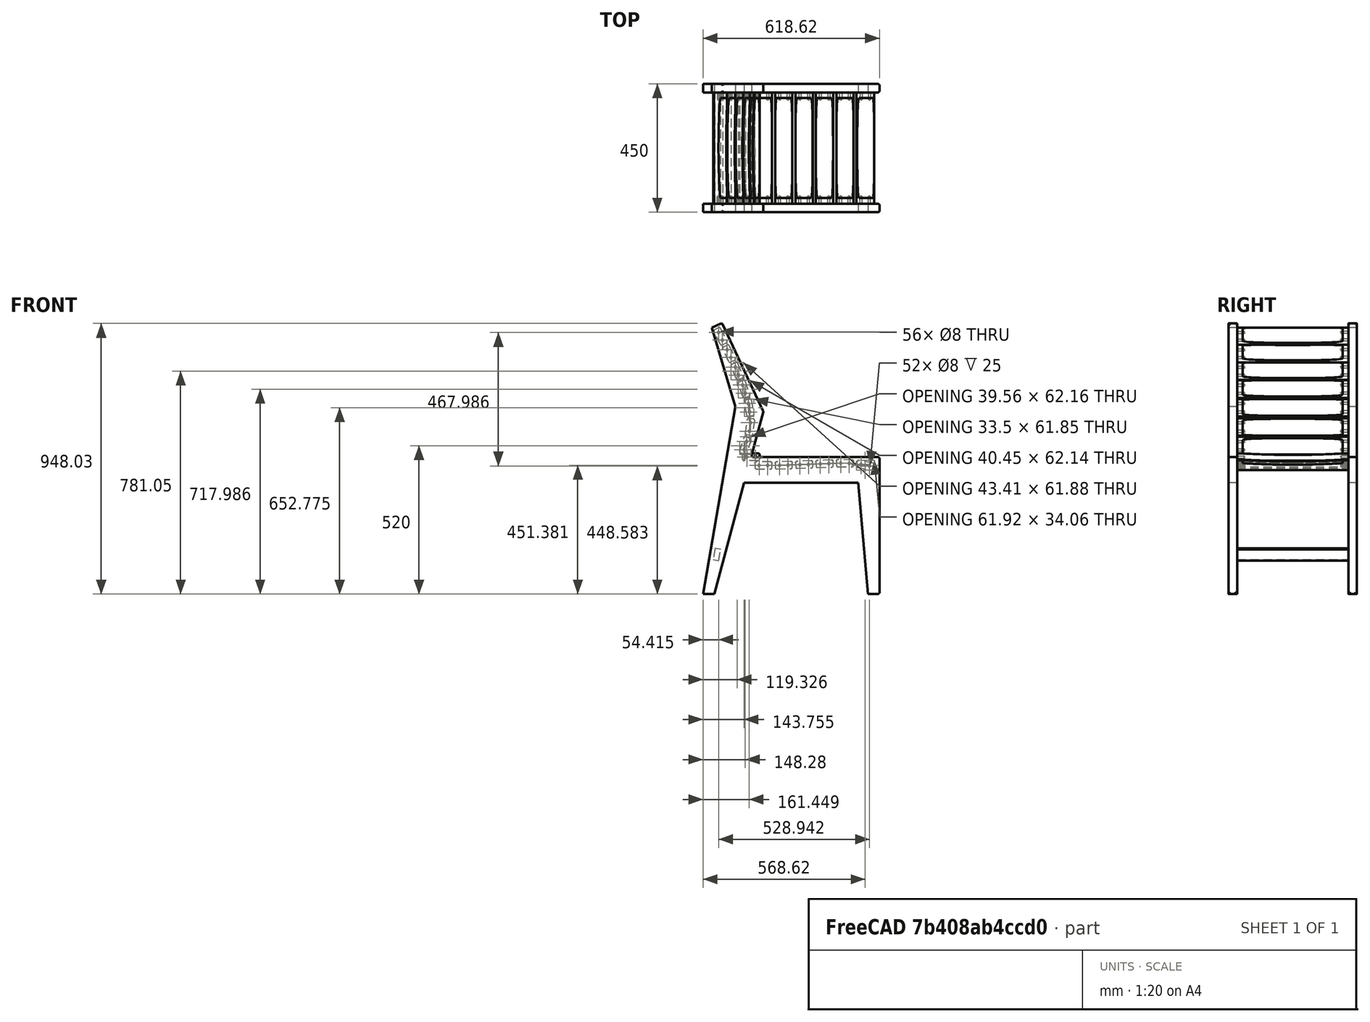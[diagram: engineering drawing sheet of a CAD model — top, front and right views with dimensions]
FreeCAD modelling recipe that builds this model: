
FCSTD DOCUMENT  (FreeCAD 0.21R33771 (Git))
Label: office_v2
License: All rights reserved
LicenseURL: http://en.wikipedia.org/wiki/All_rights_reserved
objects: TechDraw::DrawViewDimension×39, Sketcher::SketchObject×8, PartDesign::Body×4, TechDraw::DrawProjGroupItem×4, PartDesign::Pad×3, Part::FeaturePython×3, TechDraw::DrawSVGTemplate×3, TechDraw::DrawPage×3, PartDesign::Hole×2, PartDesign::SubShapeBinder×2, TechDraw::DrawProjGroup×2, TechDraw::DrawViewBalloon×2, Spreadsheet::Sheet×1, PartDesign::Fillet×1, PartDesign::Pocket×1, TechDraw::DrawViewPart×1, App::Part×1, PartDesign::Boolean×1
note: 92 computed .brp shape members not serialized (recipe doc carries the construction recipe); baked Part::Feature solids carry a one-line shape summary decoded from their .brp

FEATURE [Sketcher::SketchObject] Sketch  label="SideSketch"
  FullyConstrained = true
  Placement = pos=(0,0,0) rot=(1,0,0;1.5708rad)
  expr: Constraints[23] = <<Spreadsheet>>.back_angle
  expr: Constraints[24] = <<Spreadsheet>>.back_leg_angle
  expr: Constraints[29] = <<Spreadsheet>>.seat_length
  expr: Constraints[30] = <<Spreadsheet>>.lumbar_end_height
  expr: Constraints[32] = <<Spreadsheet>>.total_height
  expr: Constraints[5] = <<Spreadsheet>>.seat_height
  sketch-geometry (28):
    g0: LineSegment StartX=0 StartY=0 StartZ=0 EndX=450 EndY=0 EndZ=0
    g1: LineSegment StartX=375.879 StartY=-90 StartZ=0 EndX=-24.1154 EndY=-90 EndZ=0
    g2: LineSegment StartX=450 StartY=0 StartZ=0 EndX=450 EndY=-480 EndZ=0
    g3: LineSegment StartX=450 StartY=-480 StartZ=0 EndX=410 EndY=-480 EndZ=0
    g4: LineSegment StartX=410 StartY=-480 StartZ=0 EndX=368.005 EndY=0 EndZ=0
    g5: LineSegment StartX=-168.616 StartY=-480 StartZ=0 EndX=-128.616 EndY=-480 EndZ=0
    g6: LineSegment StartX=-101.684 StartY=470 StartZ=0 EndX=-137.936 EndY=453.095 EndZ=0
    g7: LineSegment StartX=-137.936 StartY=453.095 StartZ=0 EndX=-55.6825 EndY=176.942 EndZ=0
    g8: LineSegment StartX=-168.616 StartY=-480 StartZ=0 EndX=-55.6825 EndY=176.942 EndZ=0
    g9: LineSegment StartX=-55.6825 StartY=176.942 StartZ=0 EndX=42.8719 EndY=160 EndZ=0
    g10: LineSegment StartX=-128.616 StartY=-480 StartZ=0 EndX=42.8719 EndY=160 EndZ=0
    g11: LineSegment StartX=-101.684 StartY=470 StartZ=0 EndX=42.8719 EndY=160 EndZ=0
    g12: LineSegment StartX=-137.936 StartY=453.095 StartZ=0 EndX=-101.684 EndY=470 EndZ=0
    g13: LineSegment StartX=-101.684 StartY=470 StartZ=0 EndX=42.8719 EndY=160 EndZ=0
    g14: LineSegment StartX=42.8719 StartY=160 StartZ=0 EndX=0 EndY=0 EndZ=0
    g15: LineSegment StartX=0 StartY=0 StartZ=0 EndX=450 EndY=0 EndZ=0
    g16: LineSegment StartX=450 StartY=0 StartZ=0 EndX=450 EndY=-480 EndZ=0
    g17: LineSegment StartX=450 StartY=-480 StartZ=0 EndX=410 EndY=-480 EndZ=0
    g18: LineSegment StartX=410 StartY=-480 StartZ=0 EndX=375.879 EndY=-90 EndZ=0
    g19: LineSegment StartX=375.879 StartY=-90 StartZ=0 EndX=-24.1154 EndY=-90 EndZ=0
    g20: LineSegment StartX=-24.1154 StartY=-90 StartZ=0 EndX=-128.616 EndY=-480 EndZ=0
    g21: LineSegment StartX=-128.616 StartY=-480 StartZ=0 EndX=-168.616 EndY=-480 EndZ=0
    g22: LineSegment StartX=-168.616 StartY=-480 StartZ=0 EndX=-55.6825 EndY=176.942 EndZ=0
    g23: LineSegment StartX=-55.6825 StartY=176.942 StartZ=0 EndX=-137.936 EndY=453.095 EndZ=0
    g24: LineSegment StartX=-125.99 StartY=-320.578 StartZ=0 EndX=-106.279 EndY=-323.967 EndZ=0
    g25: LineSegment StartX=-106.279 StartY=-323.967 StartZ=0 EndX=-113.056 EndY=-363.388 EndZ=0
    g26: LineSegment StartX=-113.056 StartY=-363.388 StartZ=0 EndX=-132.767 EndY=-360 EndZ=0
    g27: LineSegment StartX=-132.767 StartY=-360 StartZ=0 EndX=-125.99 EndY=-320.578 EndZ=0
  constraints (75):
    c: Horizontal(g0)
    c: Horizontal(g1)
    c: Coincident(g2,g3)
    c: Horizontal(g3)
    c: Coincident(g4,g3)
    c: DistanceY(g2,g0) = 480
    c: PointOnObject(g5,g3)
    c: Coincident(g2,g0)
    c: Perpendicular(g2,g0)
    c: DistanceX(g3,g2) = 40
    c: Angle(g1,g4) = 1.65806
    c: Horizontal(g5)
    c: DistanceY(g1,g0) = 90
    c: Coincident(g7,g6)
    c: Coincident(g8,g5)
    c: DistanceX(g5,g5) = 40
    c: Coincident(g7,g8)
    c: Coincident(g9,g7)
    c: Angle(g8,g9) = 1.5708
    c: Coincident(g10,g5)
    c: Coincident(g11,g6)
    c: Coincident(g11,g10)
    c: Coincident(g10,g9)
    c: Angle(g0,g11) = 2.00713
    c: Angle(g10,g1) = 1.8326
    c: PointOnObject(g0,g10)
    c: PointOnObject(g1,g10)
    c: Perpendicular(g11,g6)
    c: Coincident(g0,g-1)
    c: Distance(g0) = 450
    c: Distance(g9,g0) = 160
    c: Distance(g9) = 100
    c: DistanceY(g5,g6) = 950
    c: Equal(g6,g5)
    c: PointOnObject(g4,g0)
    c: PointOnObject(g1,g4)
    c: Coincident(g6,g12)
    c: Coincident(g12,g6)
    c: Coincident(g12,g13)
    c: Coincident(g13,g9)
    c: Coincident(g13,g14)
    c: Coincident(g14,g0)
    c: Coincident(g14,g15)
    c: Coincident(g15,g0)
    c: Coincident(g15,g16)
    c: Coincident(g16,g2)
    c: Coincident(g16,g17)
    c: Coincident(g17,g3)
    c: Coincident(g17,g18)
    c: Coincident(g18,g1)
    c: Coincident(g18,g19)
    c: Coincident(g19,g1)
    c: Coincident(g19,g20)
    c: Coincident(g20,g5)
    c: Coincident(g20,g21)
    c: Coincident(g21,g5)
    c: Coincident(g21,g22)
    c: Coincident(g22,g7)
    c: Coincident(g22,g23)
    c: Coincident(g23,g12)
    c: Coincident(g24,g25)
    c: Coincident(g25,g26)
    c: Coincident(g26,g27)
    c: Coincident(g27,g24)
    c: Perpendicular(g25,g24)
    c: Perpendicular(g26,g25)
    c: Perpendicular(g26,g27)
    c: Parallel(g27,g22)
    c: Distance(g24,g22) = 15
    c: Distance(g25) = 40
    c: DistanceY(g20,g26) = 120
    c: Distance(g26) = 20
    c: Angle(g12,g13) = 1.5708
    c: Angle(g13,g9) = 0.964221
    c: Angle(g9,g23) = 2.03053
FEATURE [Spreadsheet::Sheet] Spreadsheet
  cells = A1='seat length; B1(seat_length)=450; A2='seat height; B2(seat_height)=480; A3='back angle; B3(back_angle)=115; A4='chair width; B4(chair_width)=450; A5='slats thickness; B5(slat_thickness)=25; A6='back slats height; B6(back_slat_width)=60; A7='seat slats width; B7(seat_slat_width)=80; A8='seat slats thickness; B8(seat_slat_thickness)=20; A9='total height; B9(total_height)=950; A10='lumbar support end height; B10(lumbar_end_height)=160; A11='back slat gap; B11(back_slat_gap)=15; A12='back slat thickness; B12(back_slat_thickness)=20; A13='seat slat gap; B13(seat_slat_gap)=10; A14='back leg angle to surface; B14(back_leg_angle)=105; A15='draft back; B15(draft_back)=5; A16='side thickness; B16(side_thickness)=30; A17='slat_width; B17(slat_width)=60; A18='slat_chamfer_radius; B18(slat_chamfer_radius)=5
FEATURE [PartDesign::Pad] Pad
  Direction = (0,-1,2e-16)
  Length = 30
  Length2 = 10
  Placement = pos=(0,0,0) rot=(1,0,0;1.5708rad)
  Profile = -> Sketch
  ReferenceAxis = -> Sketch [N_Axis]
  Type = 0
  expr: Length = <<Spreadsheet>>.side_thickness
FEATURE [PartDesign::Fillet] Fillet
  Base = -> Pad [Face2,Face3,Face4,Face5]
  BaseFeature = -> Pad
  Placement = pos=(0,0,0) rot=(1,0,0;1.5708rad)
  Radius = 6
  SupportTransform = false
  UseAllEdges = false
FEATURE [PartDesign::Body] Body  label="LeftSide"
  Group = -> [Sketch,Pad,Fillet]
  Origin = -> Origin
  Tip = -> Fillet
FEATURE [Sketcher::SketchObject] Sketch001  label="curves"
  ExternalGeometry = -> [Sketch]
  FullyConstrained = false
  MapMode = 5
  Placement = pos=(0,-1.72e-14,0) rot=(-1,0,0;1.5708rad)
  Support = -> [Pad]
  sketch-geometry (23):
    g0: LineSegment StartX=375.879 StartY=90 StartZ=0 EndX=368.005 EndY=0 EndZ=0
    g1: LineSegment StartX=0 StartY=0 StartZ=0 EndX=-24.1154 EndY=90 EndZ=0
    g2: LineSegment StartX=42.8719 StartY=-160 StartZ=0 EndX=-55.6825 EndY=-176.942 EndZ=0
    g3: Circle CenterX=-107.436 CenterY=-423.182 CenterZ=0 NormalX=0 NormalY=0 NormalZ=1 AngleXU=0 Radius=1
    g4: Circle CenterX=4.19663 CenterY=-116.283 CenterZ=0 NormalX=0 NormalY=0 NormalZ=1 AngleXU=0 Radius=1
    g5: Circle CenterX=-20.3403 CenterY=-40 CenterZ=0 NormalX=0 NormalY=0 NormalZ=1 AngleXU=0 Radius=1
    g6: BSplineCurve PolesCount=6 KnotsCount=4 Degree=3 IsPeriodic=0
    g7: GeomPoint X=-107.436 Y=-423.182 Z=0
    g8: GeomPoint X=-6.41239 Y=-168.472 Z=0
    g9: GeomPoint X=-20.3403 Y=-40 Z=0
    g10: Circle CenterX=-67.1086 CenterY=-343.425 CenterZ=0 NormalX=0 NormalY=0 NormalZ=1 AngleXU=0 Radius=0.962105
    g11: Circle CenterX=-16.1135 CenterY=-229.617 CenterZ=0 NormalX=0 NormalY=0 NormalZ=1 AngleXU=0 Radius=0.629843
    g12: Circle CenterX=-5.01988 CenterY=-156.601 CenterZ=0 NormalX=0 NormalY=0 NormalZ=1 AngleXU=0 Radius=1
    g13: GeomPoint X=-31.7882 Y=-257.283 Z=0
    g14: Circle CenterX=400 CenterY=28.6187 CenterZ=0 NormalX=0 NormalY=0 NormalZ=1 AngleXU=0 Radius=1
    g15: Circle CenterX=43.0206 CenterY=29.1813 CenterZ=0 NormalX=0 NormalY=0 NormalZ=1 AngleXU=0 Radius=1
    g16: BSplineCurve PolesCount=5 KnotsCount=3 Degree=3 IsPeriodic=0
    g17: GeomPoint X=400 Y=28.6187 Z=0
    g18: GeomPoint X=43.0206 Y=29.1813 Z=0
    g19: Circle CenterX=358.23 CenterY=20.6863 CenterZ=0 NormalX=0 NormalY=0 NormalZ=1 AngleXU=0 Radius=1
    g20: Circle CenterX=277.297 CenterY=21.6556 CenterZ=0 NormalX=0 NormalY=0 NormalZ=1 AngleXU=0 Radius=1
    g21: Circle CenterX=111.923 CenterY=30.2855 CenterZ=0 NormalX=0 NormalY=0 NormalZ=1 AngleXU=0 Radius=1
    g22: GeomPoint X=274.038 Y=22.8992 Z=0
  constraints (40):
    c: Coincident(g0,g-6)
    c: Parallel(g0,g-5)
    c: Coincident(g1,g-14)
    c: Coincident(g1,g-7)
    c: PointOnObject(g0,g-14)
    c: Coincident(g2,g-13)
    c: Coincident(g2,g-10)
    c: Weight(g3) = 1
    c: Equal(g3,g4)
    c: Equal(g3,g5)
    c: InternalAlignment(g3,g6)
    c: InternalAlignment(g4,g6)
    c: InternalAlignment(g5,g6)
    c: InternalAlignment(g7,g6)
    c: InternalAlignment(g8,g6)
    c: InternalAlignment(g9,g6)
    c: Distance(g6,g-11) = 40
    c: DistanceY(g-1,g6) = -40
    c: InternalAlignment(g10,g6)
    c: InternalAlignment(g11,g6)
    c: InternalAlignment(g12,g6)
    c: Equal(g12,g3)
    c: InternalAlignment(g13,g6)
    c: Distance(g6,g-12) = 25
    c: Distance(g6,g-13) = 30
    c: PointOnObject(g8,g2)
    c: Weight(g14) = 1
    c: Equal(g14,g15)
    c: InternalAlignment(g14,g16)
    c: InternalAlignment(g15,g16)
    c: InternalAlignment(g17,g16)
    c: InternalAlignment(g18,g16)
    c: Distance(g16,g-3) = 50
    c: InternalAlignment(g19,g16)
    c: Equal(g19,g14)
    c: InternalAlignment(g20,g16)
    c: Equal(g20,g14)
    c: InternalAlignment(g21,g16)
    c: Equal(g21,g14)
    c: InternalAlignment(g22,g16)
FEATURE [Sketcher::SketchObject] Sketch002  label="slat_profile"
  FullyConstrained = true
  MapMode = 5
  Placement = pos=(0,0,0) rot=(1,0,0;1.5708rad)
  Support = -> [XZ_Plane001]
  expr: Constraints[15] = <<Spreadsheet>>.slat_width
  expr: Constraints[16] = <<Spreadsheet>>.slat_thickness
  expr: Constraints[17] = <<Spreadsheet>>.slat_chamfer_radius
  sketch-geometry (9):
    g0: ArcOfCircle CenterX=25 CenterY=-7.5 CenterZ=0 NormalX=0 NormalY=0 NormalZ=1 AngleXU=0 Radius=5 StartAngle=4.71239 EndAngle=6.28319
    g1: LineSegment StartX=25 StartY=-12.5 StartZ=0 EndX=-25 EndY=-12.5 EndZ=0
    g2: ArcOfCircle CenterX=-25 CenterY=-7.5 CenterZ=0 NormalX=0 NormalY=0 NormalZ=1 AngleXU=0 Radius=5 StartAngle=3.14159 EndAngle=4.71239
    g3: LineSegment StartX=-30 StartY=-7.5 StartZ=0 EndX=-30 EndY=7.5 EndZ=0
    g4: ArcOfCircle CenterX=-25 CenterY=7.5 CenterZ=0 NormalX=0 NormalY=0 NormalZ=1 AngleXU=0 Radius=5 StartAngle=1.5708 EndAngle=3.14159
    g5: LineSegment StartX=-25 StartY=12.5 StartZ=0 EndX=25 EndY=12.5 EndZ=0
    g6: ArcOfCircle CenterX=25 CenterY=7.5 CenterZ=0 NormalX=0 NormalY=0 NormalZ=1 AngleXU=0 Radius=5 StartAngle=1e-16 EndAngle=1.5708
    g7: LineSegment StartX=30 StartY=7.5 StartZ=0 EndX=30 EndY=-7.5 EndZ=0
    g8: GeomPoint X=-30 Y=12.5 Z=0
  constraints (20):
    c: Tangent(g0,g1) = 1.5708
    c: Tangent(g1,g2) = 1.5708
    c: Tangent(g2,g3) = 1.5708
    c: Tangent(g3,g4) = 1.5708
    c: Tangent(g4,g5) = 1.5708
    c: Tangent(g5,g6) = 1.5708
    c: Tangent(g6,g7) = 1.5708
    c: Tangent(g7,g0) = 1.5708
    c: Equal(g0,g2)
    c: Equal(g2,g4)
    c: Equal(g4,g6)
    c: PointOnObject(g8,g3)
    c: PointOnObject(g8,g5)
    c: Parallel(g5,g1)
    c: Perpendicular(g1,g7)
    c: Distance(g6,g3) = 60
    c: Distance(g1,g4) = 25
    c: Distance(g2,g2) = 5
    c: Symmetric(g3,g6,g-2)
    c: Symmetric(g5,g0,g-1)
FEATURE [PartDesign::Pad] Pad001
  Direction = (0,-1,-2e-16)
  Length = 390
  Length2 = 10
  Placement = pos=(0,0,0) rot=(1,0,0;1.5708rad)
  Profile = -> Sketch002
  ReferenceAxis = -> Sketch002 [N_Axis]
  Reversed = true
  Type = 0
  expr: Length = <<Spreadsheet>>.chair_width - <<Spreadsheet>>.side_thickness * 2
FEATURE [Sketcher::SketchObject] Sketch003
  ExternalGeometry = -> [Pad001]
  FullyConstrained = true
  MapMode = 5
  Placement = pos=(0,0,0) rot=(1,0,0;1.5708rad)
  Support = -> [Pad001]
  expr: Constraints[0] = <<Spreadsheet>>.slat_thickness / 2
  sketch-geometry (2):
    g0: Circle CenterX=15 CenterY=-7.1e-15 CenterZ=0 NormalX=0 NormalY=0 NormalZ=1 AngleXU=0 Radius=4
    g1: Circle CenterX=-15 CenterY=0 CenterZ=0 NormalX=0 NormalY=0 NormalZ=1 AngleXU=0 Radius=4
  constraints (7):
    c: Distance(g0,g-3) = 12.5
    c: Distance(g0,g-4) = 15
    c: Diameter(g0) = 8
    c: Diameter(g1) = 8
    c: PointOnObject(g1,g-1)
    c: Distance(g1,g-5) = 15
    c: Distance(g1,g0) = 30
FEATURE [PartDesign::Hole] Hole
  BaseFeature = -> Pad001
  CustomThreadClearance = 0
  Depth = 25
  DepthType = 0
  Diameter = 8
  DrillForDepth = false
  DrillPoint = 1
  DrillPointAngle = 118
  HoleCutCountersinkAngle = 90
  HoleCutCustomValues = false
  HoleCutDepth = 0
  HoleCutDiameter = 6.1
  HoleCutType = 0
  ModelThread = false
  Placement = pos=(0,0,0) rot=(1,0,0;1.5708rad)
  Profile = -> Sketch003
  Tapered = false
  TaperedAngle = 90
  ThreadClass = 0
  ThreadDepth = 25
  ThreadDepthType = 0
  ThreadDirection = 0
  ThreadFit = 0
  ThreadSize = 0
  ThreadType = 0
  Threaded = false
  UseCustomThreadClearance = false
FEATURE [PartDesign::SubShapeBinder] Binder
  BindCopyOnChange = 0
  BindMode = 0
  ClaimChildren = false
  Context = -> Body001 [Binder.]
  Fuse = false
  MakeFace = true
  OffsetFill = false
  OffsetIntersection = false
  OffsetJoinType = 0
  OffsetOpenResult = false
  PartialLoad = false
  Relative = true
  Support = -> [Body]
  _Version = 2
FEATURE [Sketcher::SketchObject] Sketch004
  ExternalGeometry = -> [Hole]
  FullyConstrained = true
  MapMode = 5
  Placement = pos=(0,390,0) rot=(-1,0,0;1.5708rad)
  Support = -> [Hole]
  sketch-geometry (2):
    g0: Circle CenterX=-15 CenterY=0 CenterZ=0 NormalX=0 NormalY=0 NormalZ=1 AngleXU=0 Radius=4
    g1: Circle CenterX=15 CenterY=0 CenterZ=0 NormalX=0 NormalY=0 NormalZ=1 AngleXU=0 Radius=4
  constraints (6):
    c: PointOnObject(g0,g-1)
    c: PointOnObject(g1,g-1)
    c: Diameter(g0) = 8
    c: Diameter(g1) = 8
    c: Distance(g1,g-4) = 15
    c: Distance(g0,g-6) = 15
FEATURE [PartDesign::Hole] Hole001
  BaseFeature = -> Hole
  CustomThreadClearance = 0
  Depth = 25
  DepthType = 0
  Diameter = 8
  DrillForDepth = false
  DrillPoint = 1
  DrillPointAngle = 118
  HoleCutCountersinkAngle = 90
  HoleCutCustomValues = false
  HoleCutDepth = 0
  HoleCutDiameter = 6.1
  HoleCutType = 0
  ModelThread = false
  Placement = pos=(0,0,0) rot=(1,0,0;1.5708rad)
  Profile = -> Sketch004
  Tapered = false
  TaperedAngle = 90
  ThreadClass = 0
  ThreadDepth = 25
  ThreadDepthType = 0
  ThreadDirection = 0
  ThreadFit = 0
  ThreadSize = 0
  ThreadType = 0
  Threaded = false
  UseCustomThreadClearance = false
FEATURE [Part::FeaturePython] Clone  label="RightSide"  # Draft clone (typed FeaturePython)
  AttacherType = Attacher::AttachEngine3D
  Fuse = false
  Objects = -> [Body]
  Placement = pos=(0,420,0) rot=(0,0,1;0rad)
  Scale = (1,1,1)
  expr: .Placement.Base.y = <<Spreadsheet>>.chair_width - <<Spreadsheet>>.side_thickness
FEATURE [Sketcher::SketchObject] Sketch005
  ExternalGeometry = -> [Hole001]
  FullyConstrained = true
  MapMode = 5
  Placement = pos=(30,0,0) rot=(0.707107,0,0.707107;3.14159rad)
  Support = -> [Hole001]
  sketch-geometry (4):
    g0: GeomPoint X=12.5 Y=-20 Z=0
    g1: GeomPoint X=12.5 Y=-370 Z=0
    g2: ArcOfCircle CenterX=3072.5 CenterY=-195 CenterZ=0 NormalX=0 NormalY=0 NormalZ=1 AngleXU=0 Radius=3065 StartAngle=3.08447 EndAngle=3.19872
    g3: LineSegment StartX=12.5 StartY=-20 StartZ=0 EndX=12.5 EndY=-370 EndZ=0
  constraints (9):
    c: PointOnObject(g0,g-3)
    c: PointOnObject(g1,g-3)
    c: Distance(g0,g-3) = 20
    c: Distance(g1,g-3) = 20
    c: Coincident(g2,g0)
    c: Coincident(g2,g1)
    c: Tangent(g2,g-4)
    c: Coincident(g3,g2)
    c: Coincident(g3,g2)
FEATURE [PartDesign::Pocket] Pocket
  BaseFeature = -> Hole001
  Direction = (-1,0,2e-16)
  Length = 64
  Length2 = 5
  Placement = pos=(0,0,0) rot=(1,0,0;1.5708rad)
  Profile = -> Sketch005
  ReferenceAxis = -> Sketch005 [N_Axis]
  Type = 4
FEATURE [PartDesign::Body] Body001  label="Slat"
  Group = -> [Sketch002,Pad001,Sketch003,Hole,Binder,Sketch001,Sketch004,Hole001,Sketch005,Pocket]
  Origin = -> Origin001
  Tip = -> Pocket
FEATURE [PartDesign::SubShapeBinder] Binder001
  BindCopyOnChange = 0
  BindMode = 0
  ClaimChildren = false
  Context = -> Body003 [Boolean.Body002.Binder001.]
  Fuse = false
  MakeFace = true
  OffsetFill = false
  OffsetIntersection = false
  OffsetJoinType = 0
  OffsetOpenResult = false
  PartialLoad = false
  Relative = true
  Support = -> [Body[Fillet.Face2]]
  _Version = 2
FEATURE [Sketcher::SketchObject] Sketch006
  ExternalGeometry = -> [Binder001]
  FullyConstrained = true
  MapMode = 5
  Placement = pos=(0,0,0) rot=(1,0,0;1.5708rad)
  Support = -> [XZ_Plane002]
  sketch-geometry (4):
    g0: LineSegment StartX=-106.279 StartY=-323.967 StartZ=0 EndX=-125.99 EndY=-320.578 EndZ=0
    g1: LineSegment StartX=-125.99 StartY=-320.578 StartZ=0 EndX=-132.767 EndY=-360 EndZ=0
    g2: LineSegment StartX=-132.767 StartY=-360 StartZ=0 EndX=-113.056 EndY=-363.388 EndZ=0
    g3: LineSegment StartX=-113.056 StartY=-363.388 StartZ=0 EndX=-106.279 EndY=-323.967 EndZ=0
  constraints (12):
    c: Coincident(g0,g1)
    c: Coincident(g1,g2)
    c: Coincident(g2,g3)
    c: Coincident(g3,g0)
    c: Distance(g1) = 40
    c: Distance(g0) = 20
    c: Parallel(g0,g2)
    c: Parallel(g3,g1)
    c: Parallel(g1,g-3)
    c: Perpendicular(g2,g3)
    c: DistanceY(g-5,g1) = 120
    c: Distance(g1,g-3) = 15
FEATURE [PartDesign::Pad] Pad002
  Direction = (0,-1,-2e-16)
  Length = 390
  Length2 = 10
  Placement = pos=(0,0,0) rot=(1,0,0;1.5708rad)
  Profile = -> Sketch006
  ReferenceAxis = -> Sketch006 [N_Axis]
  Reversed = true
  Type = 0
  expr: Length = <<Spreadsheet>>.chair_width - 2 * <<Spreadsheet>>.side_thickness
FEATURE [PartDesign::Body] Body002  label="Stretcher"
  Group = -> [Binder001,Sketch006,Pad002]
  Origin = -> Origin002
  Tip = -> Pad002
FEATURE [Part::FeaturePython] PathArray001  label="SeatSlats"  # WARN: FeaturePython — macro-defined, semantics opaque (R4)
  Align = true
  AlignMode = 2
  Base = -> Pocket
  Count = 6
  EndOffset = 0
  ExtraTranslation = (0,0,0)
  ForceVertical = true
  PathObject = -> Sketch001
  PathSubelements = -> [Sketch001]
  Placement = pos=(0,390,0) rot=(0,0,1;0rad)
  StartOffset = 0
  TangentVector = (1,0,0)
  VerticalVector = (0,0,1)
  expr: .Placement.Base.y = <<Spreadsheet>>.chair_width - 2 * <<Spreadsheet>>.side_thickness
FEATURE [Part::FeaturePython] PathArray  label="BackSlats"  # WARN: FeaturePython — macro-defined, semantics opaque (R4)
  Align = true
  AlignMode = 0
  Base = -> Pocket
  Count = 7
  EndOffset = 0
  ExtraTranslation = (0,0,0)
  ForceVertical = false
  PathObject = -> Sketch001
  PathSubelements = -> [Sketch001]
  StartOffset = 0
  TangentVector = (1,0,0)
  VerticalVector = (0,0,1)
FEATURE [TechDraw::DrawSVGTemplate] Template
  Height = 594
  Orientation = 1
  Template = <path>
  Width = 841
FEATURE [TechDraw::DrawViewPart] View002
  CoarseView = false
  Direction = (0,1,0)
  Focus = 100
  HardHidden = false
  IsoCount = 0
  IsoHidden = false
  IsoVisible = false
  LockPosition = false
  Perspective = false
  Rotation = 280
  ScaleType = 0
  ScrubCount = 0
  SeamHidden = false
  SeamVisible = false
  SmoothHidden = false
  SmoothVisible = true
  Source = -> [Pad,PathArray,PathArray001]
  X = 153.16
  XDirection = (-1,0,0)
  Y = 240.179
FEATURE [TechDraw::DrawViewDimension] Dimension
  AngleOverride = false
  Arbitrary = false
  ArbitraryTolerances = false
  EqualTolerance = true
  ExtensionAngle = 0
  FormatSpec = ⌀%.2w
  FormatSpecOverTolerance = %+.2w
  FormatSpecUnderTolerance = %+.2w
  Inverted = false
  LineAngle = 0
  LockPosition = false
  MeasureType = 1
  OverTolerance = 0
  References2D = -> [View002]
  Rotation = 0
  ScaleType = 0
  TheoreticalExact = false
  Type = 5
  UnderTolerance = 0
  X = -67.7505
  Y = 256.25
FEATURE [TechDraw::DrawSVGTemplate] Template001
  Height = 215.9
  Orientation = 1
  Template = <path>
  Width = 279.4
FEATURE [TechDraw::DrawProjGroupItem] ProjItem  label="Front"
  CoarseView = false
  Direction = (1,0,0)
  Focus = 100
  HardHidden = false
  IsoCount = 0
  IsoHidden = false
  IsoVisible = false
  LockPosition = true
  Perspective = false
  Rotation = 0
  RotationVector = (0,1,0)
  Scale = 0.5
  ScaleType = 2
  ScrubCount = 0
  SeamHidden = false
  SeamVisible = false
  SmoothHidden = false
  SmoothVisible = true
  Source = -> [Pocket]
  Type = 0
  X = 0
  XDirection = (0,1,2e-16)
  Y = 0
FEATURE [TechDraw::DrawProjGroupItem] ProjItem001  label="Top"
  CoarseView = false
  Direction = (0,-2e-16,1)
  Focus = 100
  HardHidden = false
  IsoCount = 0
  IsoHidden = false
  IsoVisible = false
  LockPosition = false
  Perspective = false
  Rotation = 0
  RotationVector = (1,0,0)
  ScaleType = 2
  ScrubCount = 0
  SeamHidden = false
  SeamVisible = false
  SmoothHidden = false
  SmoothVisible = true
  Source = -> [Pocket]
  Type = 4
  X = 0
  XDirection = (0,1,2e-16)
  Y = -36.25
FEATURE [TechDraw::DrawProjGroupItem] ProjItem002  label="Left"
  CoarseView = false
  Direction = (1e-16,-1,-2e-16)
  Focus = 100
  HardHidden = false
  IsoCount = 0
  IsoHidden = false
  IsoVisible = false
  LockPosition = false
  Perspective = false
  Rotation = 0
  RotationVector = (1,0,0)
  ScaleType = 2
  ScrubCount = 0
  SeamHidden = false
  SeamVisible = false
  SmoothHidden = false
  SmoothVisible = true
  Source = -> [Pocket]
  Type = 1
  X = 127.5
  XDirection = (1,1e-16,0)
  Y = 0
FEATURE [TechDraw::DrawProjGroup] ProjGroup
  Anchor = -> ProjItem
  AutoDistribute = true
  LockPosition = false
  ProjectionType = 0
  Rotation = 0
  Scale = 0.5
  ScaleType = 2
  Source = -> [Pocket]
  Views = -> [ProjItem,ProjItem001,ProjItem002]
  X = 115.867
  Y = 123.966
  spacingX = 15
  spacingY = 15
FEATURE [TechDraw::DrawViewDimension] Dimension001
  AngleOverride = false
  Arbitrary = false
  ArbitraryTolerances = false
  EqualTolerance = true
  ExtensionAngle = 0
  FormatSpec = %.2w
  FormatSpecOverTolerance = %+.2w
  FormatSpecUnderTolerance = %+.2w
  Inverted = false
  LineAngle = 0
  LockPosition = false
  MeasureType = 1
  OverTolerance = 0
  References2D = -> [ProjItem]
  Rotation = 0
  ScaleType = 0
  TheoreticalExact = false
  Type = 1
  UnderTolerance = 0
  X = -92.9545
  Y = 15.6989
FEATURE [TechDraw::DrawViewDimension] Dimension003
  AngleOverride = false
  Arbitrary = false
  ArbitraryTolerances = false
  EqualTolerance = true
  ExtensionAngle = 0
  FormatSpec = ⌀%.2w
  FormatSpecOverTolerance = %+.2w
  FormatSpecUnderTolerance = %+.2w
  Inverted = false
  LineAngle = 0
  LockPosition = false
  MeasureType = 1
  OverTolerance = 0
  References2D = -> [ProjItem002]
  Rotation = 0
  ScaleType = 0
  TheoreticalExact = false
  Type = 5
  UnderTolerance = 0
  X = -4.33544
  Y = 3.01756
FEATURE [TechDraw::DrawViewDimension] Dimension004
  AngleOverride = false
  Arbitrary = false
  ArbitraryTolerances = false
  EqualTolerance = true
  ExtensionAngle = 0
  FormatSpec = %.2w
  FormatSpecOverTolerance = %+.2w
  FormatSpecUnderTolerance = %+.2w
  Inverted = false
  LineAngle = 0
  LockPosition = false
  MeasureType = 1
  OverTolerance = 0
  References2D = -> [ProjItem002]
  Rotation = 0
  ScaleType = 0
  TheoreticalExact = false
  Type = 1
  UnderTolerance = 0
  X = -0.367799
  Y = -20.9158
FEATURE [TechDraw::DrawViewDimension] Dimension005
  AngleOverride = false
  Arbitrary = false
  ArbitraryTolerances = false
  EqualTolerance = true
  ExtensionAngle = 0
  FormatSpec = %.2w
  FormatSpecOverTolerance = %+.2w
  FormatSpecUnderTolerance = %+.2w
  Inverted = false
  LineAngle = 0
  LockPosition = false
  MeasureType = 1
  OverTolerance = 0
  References2D = -> [ProjItem002]
  Rotation = 0
  ScaleType = 0
  TheoreticalExact = false
  Type = 2
  UnderTolerance = 0
  X = 22.7064
  Y = 2.0517
FEATURE [TechDraw::DrawViewDimension] Dimension006
  AngleOverride = false
  Arbitrary = false
  ArbitraryTolerances = false
  EqualTolerance = true
  ExtensionAngle = 0
  FormatSpec = %.2w
  FormatSpecOverTolerance = %+.2w
  FormatSpecUnderTolerance = %+.2w
  Inverted = false
  LineAngle = 0
  LockPosition = false
  MeasureType = 1
  OverTolerance = 0
  References2D = -> [ProjItem]
  Rotation = 0
  ScaleType = 0
  TheoreticalExact = false
  Type = 1
  UnderTolerance = 0
  X = 92.5
  Y = 15.0773
FEATURE [TechDraw::DrawViewDimension] Dimension007
  AngleOverride = false
  Arbitrary = false
  ArbitraryTolerances = false
  EqualTolerance = true
  ExtensionAngle = 0
  FormatSpec = %.2w
  FormatSpecOverTolerance = %+.2w
  FormatSpecUnderTolerance = %+.2w
  Inverted = false
  LineAngle = 0
  LockPosition = false
  MeasureType = 1
  OverTolerance = 0
  References2D = -> [ProjItem]
  Rotation = 0
  ScaleType = 0
  TheoreticalExact = false
  Type = 1
  UnderTolerance = 0
  X = 4.16648
  Y = -64.6611
FEATURE [TechDraw::DrawViewDimension] Dimension008
  AngleOverride = false
  Arbitrary = false
  ArbitraryTolerances = false
  EqualTolerance = true
  ExtensionAngle = 0
  FormatSpec = %.2w
  FormatSpecOverTolerance = %+.2w
  FormatSpecUnderTolerance = %+.2w
  Inverted = false
  LineAngle = 0
  LockPosition = false
  MeasureType = 1
  OverTolerance = 0
  References2D = -> [ProjItem]
  Rotation = 0
  ScaleType = 0
  TheoreticalExact = false
  Type = 2
  UnderTolerance = 0
  X = -101.291
  Y = 6.69954
FEATURE [Sketcher::SketchObject] Sketch007  label="SideSketchCopy"
  FullyConstrained = true
  Placement = pos=(0,0,0) rot=(1,0,0;1.5708rad)
  expr: Constraints[23] = <<Spreadsheet>>.back_angle
  expr: Constraints[24] = <<Spreadsheet>>.back_leg_angle
  expr: Constraints[29] = <<Spreadsheet>>.seat_length
  expr: Constraints[30] = <<Spreadsheet>>.lumbar_end_height
  expr: Constraints[32] = <<Spreadsheet>>.total_height
  expr: Constraints[5] = <<Spreadsheet>>.seat_height
  sketch-geometry (38):
    g0: LineSegment StartX=0 StartY=0 StartZ=0 EndX=450 EndY=0 EndZ=0
    g1: LineSegment StartX=375.879 StartY=-90 StartZ=0 EndX=-24.1154 EndY=-90 EndZ=0
    g2: LineSegment StartX=450 StartY=0 StartZ=0 EndX=450 EndY=-480 EndZ=0
    g3: LineSegment StartX=450 StartY=-480 StartZ=0 EndX=410 EndY=-480 EndZ=0
    g4: LineSegment StartX=410 StartY=-480 StartZ=0 EndX=368.005 EndY=0 EndZ=0
    g5: LineSegment StartX=-168.616 StartY=-480 StartZ=0 EndX=-128.616 EndY=-480 EndZ=0
    g6: LineSegment StartX=-101.684 StartY=470 StartZ=0 EndX=-137.936 EndY=453.095 EndZ=0
    g7: LineSegment StartX=-137.936 StartY=453.095 StartZ=0 EndX=-55.6825 EndY=176.942 EndZ=0
    g8: LineSegment StartX=-168.616 StartY=-480 StartZ=0 EndX=-55.6825 EndY=176.942 EndZ=0
    g9: LineSegment StartX=-55.6825 StartY=176.942 StartZ=0 EndX=42.8719 EndY=160 EndZ=0
    g10: LineSegment StartX=-128.616 StartY=-480 StartZ=0 EndX=42.8719 EndY=160 EndZ=0
    g11: LineSegment StartX=-101.684 StartY=470 StartZ=0 EndX=42.8719 EndY=160 EndZ=0
    g12: LineSegment StartX=-137.936 StartY=453.095 StartZ=0 EndX=-101.684 EndY=470 EndZ=0
    g13: LineSegment StartX=-101.684 StartY=470 StartZ=0 EndX=42.8719 EndY=160 EndZ=0
    g14: LineSegment StartX=42.8719 StartY=160 StartZ=0 EndX=0 EndY=0 EndZ=0
    g15: LineSegment StartX=0 StartY=0 StartZ=0 EndX=450 EndY=0 EndZ=0
    g16: LineSegment StartX=450 StartY=0 StartZ=0 EndX=450 EndY=-480 EndZ=0
    g17: LineSegment StartX=450 StartY=-480 StartZ=0 EndX=410 EndY=-480 EndZ=0
    g18: LineSegment StartX=410 StartY=-480 StartZ=0 EndX=375.879 EndY=-90 EndZ=0
    g19: LineSegment StartX=375.879 StartY=-90 StartZ=0 EndX=-24.1154 EndY=-90 EndZ=0
    g20: LineSegment StartX=-24.1154 StartY=-90 StartZ=0 EndX=-128.616 EndY=-480 EndZ=0
    g21: LineSegment StartX=-128.616 StartY=-480 StartZ=0 EndX=-168.616 EndY=-480 EndZ=0
    g22: LineSegment StartX=-168.616 StartY=-480 StartZ=0 EndX=-55.6825 EndY=176.942 EndZ=0
    g23: LineSegment StartX=-55.6825 StartY=176.942 StartZ=0 EndX=-137.936 EndY=453.095 EndZ=0
    g24: LineSegment StartX=-24.1154 StartY=-90 StartZ=0 EndX=3.6e-15 EndY=0 EndZ=0
    g25: LineSegment StartX=368.005 StartY=0 StartZ=0 EndX=375.879 EndY=-90 EndZ=0
    g26: LineSegment StartX=-55.6825 StartY=176.942 StartZ=0 EndX=42.8719 EndY=160 EndZ=0
    g27: LineSegment StartX=-168.616 StartY=-480 StartZ=0 EndX=-130.377 EndY=-486.573 EndZ=0
    g28: LineSegment StartX=-130.377 StartY=-486.573 StartZ=0 EndX=-128.616 EndY=-480 EndZ=0
    g29: LineSegment StartX=61.7657 StartY=230.513 StartZ=0 EndX=42.8719 EndY=160 EndZ=0
    g30: LineSegment StartX=450 StartY=0 StartZ=0 EndX=368.005 EndY=0 EndZ=0
    g31: LineSegment StartX=42.8719 StartY=160 StartZ=0 EndX=0 EndY=0 EndZ=0
    g32: LineSegment StartX=-124.296 StartY=-310.723 StartZ=0 EndX=-104.585 EndY=-314.111 EndZ=0
    g33: LineSegment StartX=-104.585 StartY=-314.111 StartZ=0 EndX=-113.056 EndY=-363.388 EndZ=0
    g34: LineSegment StartX=-113.056 StartY=-363.388 StartZ=0 EndX=-132.767 EndY=-360 EndZ=0
    g35: LineSegment StartX=-132.767 StartY=-360 StartZ=0 EndX=-124.296 EndY=-310.723 EndZ=0
    g36: LineSegment StartX=18.7802 StartY=211.665 StartZ=0 EndX=-55.6825 EndY=176.942 EndZ=0
    g37: LineSegment StartX=61.7657 StartY=230.513 StartZ=0 EndX=2.59858 EndY=246.366 EndZ=0
  constraints (96):
    c: Horizontal(g0)
    c: Horizontal(g1)
    c: Coincident(g2,g3)
    c: Horizontal(g3)
    c: Coincident(g4,g3)
    c: DistanceY(g2,g0) = 480
    c: PointOnObject(g5,g3)
    c: Coincident(g2,g0)
    c: Perpendicular(g2,g0)
    c: DistanceX(g3,g2) = 40
    c: Angle(g1,g4) = 1.65806
    c: Horizontal(g5)
    c: DistanceY(g1,g0) = 90
    c: Coincident(g7,g6)
    c: Coincident(g8,g5)
    c: DistanceX(g5,g5) = 40
    c: Coincident(g7,g8)
    c: Coincident(g9,g7)
    c: Angle(g8,g9) = 1.5708
    c: Coincident(g10,g5)
    c: Coincident(g11,g6)
    c: Coincident(g11,g10)
    c: Coincident(g10,g9)
    c: Angle(g0,g11) = 2.00713
    c: Angle(g10,g1) = 1.8326
    c: PointOnObject(g0,g10)
    c: PointOnObject(g1,g10)
    c: Perpendicular(g11,g6)
    c: Coincident(g0,g-1)
    c: Distance(g0) = 450
    c: Distance(g9,g0) = 160
    c: Distance(g9) = 100
    c: DistanceY(g5,g6) = 950
    c: Equal(g6,g5)
    c: PointOnObject(g4,g0)
    c: PointOnObject(g1,g4)
    c: Coincident(g6,g12)
    c: Coincident(g12,g6)
    c: Coincident(g12,g13)
    c: Coincident(g13,g9)
    c: Coincident(g13,g14)
    c: Coincident(g14,g0)
    c: Coincident(g14,g15)
    c: Coincident(g15,g0)
    c: Coincident(g15,g16)
    c: Coincident(g16,g2)
    c: Coincident(g16,g17)
    c: Coincident(g17,g3)
    c: Coincident(g17,g18)
    c: Coincident(g18,g1)
    c: Coincident(g18,g19)
    c: Coincident(g19,g1)
    c: Coincident(g19,g20)
    c: Coincident(g20,g5)
    c: Coincident(g20,g21)
    c: Coincident(g21,g5)
    c: Coincident(g21,g22)
    c: Coincident(g22,g7)
    c: Coincident(g22,g23)
    c: Coincident(g23,g12)
    c: Coincident(g24,g19)
    c: Coincident(g24,g14)
    c: Coincident(g25,g4)
    c: Coincident(g25,g18)
    c: Coincident(g26,g22)
    c: Coincident(g26,g13)
    c: Coincident(g21,g27)
    c: Coincident(g27,g28)
    c: Coincident(g28,g20)
    c: Parallel(g26,g27)
    c: Parallel(g28,g20)
    c: Coincident(g29,g13)
    c: Coincident(g30,g15)
    c: Coincident(g30,g25)
    c: Coincident(g31,g13)
    c: Coincident(g31,g14)
    c: Coincident(g32,g33)
    c: Coincident(g33,g34)
    c: Coincident(g34,g35)
    c: Coincident(g35,g32)
    c: Perpendicular(g32,g35)
    c: Perpendicular(g33,g32)
    c: Perpendicular(g34,g33)
    c: Distance(g33) = 50
    c: Distance(g32) = 20
    c: Parallel(g35,g22)
    c: Distance(g34,g22) = 15
    c: DistanceY(g21,g34) = 120
    c: PointOnObject(g36,g13)
    c: Coincident(g36,g22)
    c: Perpendicular(g13,g36)
    c: Parallel(g14,g29)
    c: Coincident(g37,g29)
    c: PointOnObject(g37,g13)
    c: Perpendicular(g29,g37)
    c: Distance(g29) = 73
FEATURE [TechDraw::DrawSVGTemplate] Template002
  Height = 215.9
  Orientation = 1
  Template = <path>
  Width = 279.4
FEATURE [TechDraw::DrawProjGroupItem] ProjItem003  label="Side: cuts and assembly"
  CoarseView = false
  Direction = (0,1,0)
  Focus = 100
  HardHidden = false
  IsoCount = 0
  IsoHidden = false
  IsoVisible = false
  LockPosition = true
  Perspective = false
  Rotation = 0
  RotationVector = (1,0,0)
  Scale = 0.25
  ScaleType = 2
  ScrubCount = 0
  SeamHidden = false
  SeamVisible = false
  SmoothHidden = false
  SmoothVisible = true
  Source = -> [Sketch007]
  Type = 0
  X = 0
  XDirection = (-2e-16,0,1)
  Y = 0
FEATURE [TechDraw::DrawProjGroup] ProjGroup001
  Anchor = -> ProjItem003
  AutoDistribute = true
  LockPosition = false
  ProjectionType = 0
  Rotation = 0
  Scale = 0.25
  ScaleType = 2
  Source = -> [Sketch007]
  Views = -> [ProjItem003]
  X = 139.7
  Y = 107.95
  spacingX = 15
  spacingY = 15
FEATURE [TechDraw::DrawViewDimension] Dimension009
  AngleOverride = false
  Arbitrary = false
  ArbitraryTolerances = false
  EqualTolerance = true
  ExtensionAngle = 0
  FormatSpec = %.2w
  FormatSpecOverTolerance = %+.2w
  FormatSpecUnderTolerance = %+.2w
  Inverted = false
  LineAngle = 0
  LockPosition = false
  MeasureType = 1
  OverTolerance = 0
  References2D = -> [ProjItem003]
  Rotation = 0
  ScaleType = 0
  TheoreticalExact = false
  Type = 1
  UnderTolerance = 0
  X = -57.6035
  Y = 87.4336
FEATURE [TechDraw::DrawViewDimension] Dimension010
  AngleOverride = false
  Arbitrary = false
  ArbitraryTolerances = false
  EqualTolerance = true
  ExtensionAngle = 0
  FormatSpec = %.0w
  FormatSpecOverTolerance = %+.2w
  FormatSpecUnderTolerance = %+.2w
  Inverted = false
  LineAngle = 0
  LockPosition = false
  MeasureType = 1
  OverTolerance = 0
  References2D = -> [ProjItem003]
  Rotation = 0
  ScaleType = 0
  TheoreticalExact = false
  Type = 0
  UnderTolerance = 0
  X = 9.17622
  Y = 69.367
FEATURE [TechDraw::DrawViewDimension] Dimension011
  AngleOverride = false
  Arbitrary = false
  ArbitraryTolerances = false
  EqualTolerance = true
  ExtensionAngle = 0
  FormatSpec = %.2w
  FormatSpecOverTolerance = %+.2w
  FormatSpecUnderTolerance = %+.2w
  Inverted = false
  LineAngle = 0
  LockPosition = false
  MeasureType = 1
  OverTolerance = 0
  References2D = -> [ProjItem003]
  Rotation = 0
  ScaleType = 0
  TheoreticalExact = false
  Type = 6
  UnderTolerance = 0
  X = -110.966
  Y = 74.4624
FEATURE [TechDraw::DrawViewDimension] Dimension012
  AngleOverride = false
  Arbitrary = false
  ArbitraryTolerances = false
  EqualTolerance = true
  ExtensionAngle = 0
  FormatSpec = %.2w
  FormatSpecOverTolerance = %+.2w
  FormatSpecUnderTolerance = %+.2w
  Inverted = false
  LineAngle = 0
  LockPosition = false
  MeasureType = 1
  OverTolerance = 0
  References2D = -> [ProjItem003]
  Rotation = 0
  ScaleType = 0
  TheoreticalExact = false
  Type = 6
  UnderTolerance = 0
  X = -5.30021
  Y = 66.6813
FEATURE [TechDraw::DrawViewDimension] Dimension013
  AngleOverride = false
  Arbitrary = false
  ArbitraryTolerances = false
  EqualTolerance = true
  ExtensionAngle = 0
  FormatSpec = %.2w
  FormatSpecOverTolerance = %+.2w
  FormatSpecUnderTolerance = %+.2w
  Inverted = false
  LineAngle = 0
  LockPosition = false
  MeasureType = 1
  OverTolerance = 0
  References2D = -> [ProjItem003]
  Rotation = 0
  ScaleType = 0
  TheoreticalExact = false
  Type = 0
  UnderTolerance = 0
  X = -9.57407
  Y = 44.5071
FEATURE [TechDraw::DrawViewDimension] Dimension014
  AngleOverride = false
  Arbitrary = false
  ArbitraryTolerances = false
  EqualTolerance = true
  ExtensionAngle = 0
  FormatSpec = %.0w
  FormatSpecOverTolerance = %+.2w
  FormatSpecUnderTolerance = %+.2w
  Inverted = false
  LineAngle = 0
  LockPosition = false
  MeasureType = 1
  OverTolerance = 0
  References2D = -> [ProjItem003]
  Rotation = 0
  ScaleType = 0
  TheoreticalExact = false
  Type = 0
  UnderTolerance = 0
  X = -23.5859
  Y = 10.523
FEATURE [TechDraw::DrawViewDimension] Dimension015
  AngleOverride = false
  Arbitrary = false
  ArbitraryTolerances = false
  EqualTolerance = true
  ExtensionAngle = 0
  FormatSpec = %.2w
  FormatSpecOverTolerance = %+.2w
  FormatSpecUnderTolerance = %+.2w
  Inverted = false
  LineAngle = 0
  LockPosition = false
  MeasureType = 1
  OverTolerance = 0
  References2D = -> [ProjItem003]
  Rotation = 0
  ScaleType = 0
  TheoreticalExact = false
  Type = 0
  UnderTolerance = 0
  X = 42.6549
  Y = -35.5068
FEATURE [TechDraw::DrawViewDimension] Dimension016
  AngleOverride = false
  Arbitrary = false
  ArbitraryTolerances = false
  EqualTolerance = true
  ExtensionAngle = 0
  FormatSpec = %.0w
  FormatSpecOverTolerance = %+.2w
  FormatSpecUnderTolerance = %+.2w
  Inverted = false
  LineAngle = 0
  LockPosition = false
  MeasureType = 1
  OverTolerance = 0
  References2D = -> [ProjItem003]
  Rotation = 0
  ScaleType = 0
  TheoreticalExact = false
  Type = 0
  UnderTolerance = 0
  X = -34.5701
  Y = -64.0785
FEATURE [TechDraw::DrawViewDimension] Dimension017
  AngleOverride = false
  Arbitrary = false
  ArbitraryTolerances = false
  EqualTolerance = true
  ExtensionAngle = 0
  FormatSpec = %.0w
  FormatSpecOverTolerance = %+.2w
  FormatSpecUnderTolerance = %+.2w
  Inverted = false
  LineAngle = 0
  LockPosition = false
  MeasureType = 1
  OverTolerance = 0
  References2D = -> [ProjItem003]
  Rotation = 0
  ScaleType = 0
  TheoreticalExact = false
  Type = 6
  UnderTolerance = 0
  X = 35.4062
  Y = -28.042
FEATURE [TechDraw::DrawViewDimension] Dimension018
  AngleOverride = false
  Arbitrary = false
  ArbitraryTolerances = false
  EqualTolerance = true
  ExtensionAngle = 0
  FormatSpec = %.0w
  FormatSpecOverTolerance = %+.2w
  FormatSpecUnderTolerance = %+.2w
  Inverted = false
  LineAngle = 0
  LockPosition = false
  MeasureType = 1
  OverTolerance = 0
  References2D = -> [ProjItem003]
  Rotation = 0
  ScaleType = 0
  TheoreticalExact = false
  Type = 6
  UnderTolerance = 0
  X = 52.3581
  Y = -44.7756
FEATURE [TechDraw::DrawViewDimension] Dimension019
  AngleOverride = false
  Arbitrary = false
  ArbitraryTolerances = false
  EqualTolerance = true
  ExtensionAngle = 0
  FormatSpec = %.2w
  FormatSpecOverTolerance = %+.2w
  FormatSpecUnderTolerance = %+.2w
  Inverted = false
  LineAngle = 0
  LockPosition = false
  MeasureType = 1
  OverTolerance = 0
  References2D = -> [ProjItem003]
  Rotation = 0
  ScaleType = 0
  TheoreticalExact = false
  Type = 6
  UnderTolerance = 0
  X = 115.845
  Y = -60.2395
FEATURE [TechDraw::DrawViewDimension] Dimension020
  AngleOverride = false
  Arbitrary = false
  ArbitraryTolerances = false
  EqualTolerance = true
  ExtensionAngle = 0
  FormatSpec = %.0w
  FormatSpecOverTolerance = %+.2w
  FormatSpecUnderTolerance = %+.2w
  Inverted = false
  LineAngle = 0
  LockPosition = false
  MeasureType = 1
  OverTolerance = 0
  References2D = -> [ProjItem003]
  Rotation = 0
  ScaleType = 0
  TheoreticalExact = false
  Type = 6
  UnderTolerance = 0
  X = -111.366
  Y = -68.2068
FEATURE [TechDraw::DrawViewDimension] Dimension021
  AngleOverride = false
  Arbitrary = false
  ArbitraryTolerances = false
  EqualTolerance = true
  ExtensionAngle = 0
  FormatSpec = %.2w
  FormatSpecOverTolerance = %+.2w
  FormatSpecUnderTolerance = %+.2w
  Inverted = false
  LineAngle = 0
  LockPosition = false
  MeasureType = 1
  OverTolerance = 0
  References2D = -> [ProjItem003]
  Rotation = 0
  ScaleType = 0
  TheoreticalExact = false
  Type = 6
  UnderTolerance = 0
  X = -15.2572
  Y = -31.7657
FEATURE [TechDraw::DrawViewDimension] Dimension022
  AngleOverride = false
  Arbitrary = false
  ArbitraryTolerances = false
  EqualTolerance = true
  ExtensionAngle = 0
  FormatSpec = %.2w
  FormatSpecOverTolerance = %+.2w
  FormatSpecUnderTolerance = %+.2w
  Inverted = false
  LineAngle = 0
  LockPosition = false
  MeasureType = 1
  OverTolerance = 0
  References2D = -> [ProjItem003]
  Rotation = 0
  ScaleType = 0
  TheoreticalExact = false
  Type = 6
  UnderTolerance = 0
  X = -14.4235
  Y = 54.6918
FEATURE [TechDraw::DrawViewDimension] Dimension023
  AngleOverride = false
  Arbitrary = false
  ArbitraryTolerances = false
  EqualTolerance = true
  ExtensionAngle = 0
  FormatSpec = %.0w
  FormatSpecOverTolerance = %+.2w
  FormatSpecUnderTolerance = %+.2w
  Inverted = false
  LineAngle = 0
  LockPosition = false
  MeasureType = 1
  OverTolerance = 0
  References2D = -> [ProjItem003]
  Rotation = 0
  ScaleType = 0
  TheoreticalExact = false
  Type = 0
  UnderTolerance = 0
  X = 80.6475
  Y = -34.2318
FEATURE [TechDraw::DrawViewDimension] Dimension024
  AngleOverride = false
  Arbitrary = false
  ArbitraryTolerances = false
  EqualTolerance = true
  ExtensionAngle = 0
  FormatSpec = %.0w
  FormatSpecOverTolerance = %+.2w
  FormatSpecUnderTolerance = %+.2w
  Inverted = false
  LineAngle = 0
  LockPosition = false
  MeasureType = 1
  OverTolerance = 0
  References2D = -> [ProjItem003]
  Rotation = 0
  ScaleType = 0
  TheoreticalExact = false
  Type = 6
  UnderTolerance = 0
  X = 47.0265
  Y = -29.5897
FEATURE [TechDraw::DrawViewDimension] Dimension025
  AngleOverride = false
  Arbitrary = false
  ArbitraryTolerances = false
  EqualTolerance = true
  ExtensionAngle = 0
  FormatSpec = %.0w
  FormatSpecOverTolerance = %+.2w
  FormatSpecUnderTolerance = %+.2w
  Inverted = false
  LineAngle = 0
  LockPosition = false
  MeasureType = 1
  OverTolerance = 0
  References2D = -> [ProjItem003]
  Rotation = 0
  ScaleType = 0
  TheoreticalExact = false
  Type = 0
  UnderTolerance = 0
  X = 78.9976
  Y = -59.0075
FEATURE [TechDraw::DrawViewDimension] Dimension026
  AngleOverride = false
  Arbitrary = false
  ArbitraryTolerances = false
  EqualTolerance = true
  ExtensionAngle = 0
  FormatSpec = %.2w
  FormatSpecOverTolerance = %+.2w
  FormatSpecUnderTolerance = %+.2w
  Inverted = false
  LineAngle = 0
  LockPosition = false
  MeasureType = 1
  OverTolerance = 0
  References2D = -> [ProjItem003]
  Rotation = 0
  ScaleType = 0
  TheoreticalExact = false
  Type = 0
  UnderTolerance = 0
  X = 119.81
  Y = -65.1059
FEATURE [TechDraw::DrawViewDimension] Dimension027
  AngleOverride = false
  Arbitrary = false
  ArbitraryTolerances = false
  EqualTolerance = true
  ExtensionAngle = 0
  FormatSpec = %.0w
  FormatSpecOverTolerance = %+.2w
  FormatSpecUnderTolerance = %+.2w
  Inverted = false
  LineAngle = 0
  LockPosition = false
  MeasureType = 1
  OverTolerance = 0
  References2D = -> [ProjItem003]
  Rotation = 0
  ScaleType = 0
  TheoreticalExact = false
  Type = 0
  UnderTolerance = 0
  X = -121.756
  Y = -70.7358
FEATURE [TechDraw::DrawViewDimension] Dimension028
  AngleOverride = false
  Arbitrary = false
  ArbitraryTolerances = false
  EqualTolerance = true
  ExtensionAngle = 0
  FormatSpec = %.2w
  FormatSpecOverTolerance = %+.2w
  FormatSpecUnderTolerance = %+.2w
  Inverted = false
  LineAngle = 0
  LockPosition = false
  MeasureType = 1
  OverTolerance = 0
  References2D = -> [ProjItem002]
  Rotation = 0
  ScaleType = 0
  TheoreticalExact = false
  Type = 0
  UnderTolerance = 0
  X = 12.9492
  Y = -1.51352
FEATURE [TechDraw::DrawViewDimension] Dimension029
  AngleOverride = false
  Arbitrary = false
  ArbitraryTolerances = false
  EqualTolerance = true
  ExtensionAngle = 0
  FormatSpec = %.2w
  FormatSpecOverTolerance = %+.2w
  FormatSpecUnderTolerance = %+.2w
  Inverted = false
  LineAngle = 0
  LockPosition = false
  MeasureType = 1
  OverTolerance = 0
  References2D = -> [ProjItem002]
  Rotation = 0
  ScaleType = 0
  TheoreticalExact = false
  Type = 2
  UnderTolerance = 0
  X = 3.25079
  Y = 3.90041
FEATURE [TechDraw::DrawViewDimension] Dimension030
  AngleOverride = false
  Arbitrary = false
  ArbitraryTolerances = false
  EqualTolerance = true
  ExtensionAngle = 0
  FormatSpec = %.2w
  FormatSpecOverTolerance = %+.2w
  FormatSpecUnderTolerance = %+.2w
  Inverted = false
  LineAngle = 0
  LockPosition = false
  MeasureType = 1
  OverTolerance = 0
  References2D = -> [ProjItem002]
  Rotation = 0
  ScaleType = 0
  TheoreticalExact = false
  Type = 0
  UnderTolerance = 0
  X = 10.9156
  Y = 5.86312
FEATURE [TechDraw::DrawViewDimension] Dimension031
  AngleOverride = false
  Arbitrary = false
  ArbitraryTolerances = false
  EqualTolerance = true
  ExtensionAngle = 0
  FormatSpec = %.2w
  FormatSpecOverTolerance = %+.2w
  FormatSpecUnderTolerance = %+.2w
  Inverted = false
  LineAngle = 0
  LockPosition = false
  MeasureType = 1
  OverTolerance = 0
  References2D = -> [ProjItem002]
  Rotation = 0
  ScaleType = 0
  TheoreticalExact = false
  Type = 0
  UnderTolerance = 0
  X = -11.5844
  Y = -0.856552
FEATURE [TechDraw::DrawViewDimension] Dimension032
  AngleOverride = false
  Arbitrary = false
  ArbitraryTolerances = false
  EqualTolerance = true
  ExtensionAngle = 0
  FormatSpec = %.2w
  FormatSpecOverTolerance = %+.2w
  FormatSpecUnderTolerance = %+.2w
  Inverted = false
  LineAngle = 0
  LockPosition = false
  MeasureType = 1
  OverTolerance = 0
  References2D = -> [ProjItem002]
  Rotation = 0
  ScaleType = 0
  TheoreticalExact = false
  Type = 0
  UnderTolerance = 0
  X = 0.613117
  Y = -0.854124
FEATURE [TechDraw::DrawPage] Page001  label="SlatDraw"
  KeepUpdated = true
  NextBalloonIndex = 1
  ProjectionType = 0
  Template = -> Template001
  Views = -> [ProjGroup,Dimension001,Dimension003,Dimension004,Dimension005,Dimension006,Dimension007,Dimension008,Dimension028,Dimension029,Dimension030,Dimension031,Dimension032]
FEATURE [TechDraw::DrawViewDimension] Dimension033
  AngleOverride = false
  Arbitrary = false
  ArbitraryTolerances = false
  EqualTolerance = true
  ExtensionAngle = 0
  FormatSpec = %.0w
  FormatSpecOverTolerance = %+.2w
  FormatSpecUnderTolerance = %+.2w
  Inverted = false
  LineAngle = 0
  LockPosition = false
  MeasureType = 1
  OverTolerance = 0
  References2D = -> [ProjItem003]
  Rotation = 0
  ScaleType = 0
  TheoreticalExact = false
  Type = 0
  UnderTolerance = 0
  X = 15.1829
  Y = -23.5686
FEATURE [TechDraw::DrawViewBalloon] Balloon
  BubbleShape = 3
  EndType = 0
  EndTypeScale = 1
  KinkLength = 5
  LockPosition = false
  OriginX = 239.308
  OriginY = -85.6112
  Rotation = 0
  ScaleType = 0
  ShapeScale = 1
  SourceView = -> ProjItem003
  Text = Dashed lines: area left for clamping
  TextWrapLen = -1
  X = 319.308
  Y = -5.6112
FEATURE [TechDraw::DrawViewDimension] Dimension034
  AngleOverride = false
  Arbitrary = false
  ArbitraryTolerances = false
  EqualTolerance = true
  ExtensionAngle = 0
  FormatSpec = %.2w
  FormatSpecOverTolerance = %+.2w
  FormatSpecUnderTolerance = %+.2w
  Inverted = false
  LineAngle = 0
  LockPosition = false
  MeasureType = 1
  OverTolerance = 0
  References2D = -> [ProjItem003]
  Rotation = 0
  ScaleType = 0
  TheoreticalExact = false
  Type = 0
  UnderTolerance = 0
  X = -81.9035
  Y = -67.5143
FEATURE [TechDraw::DrawViewDimension] Dimension035
  AngleOverride = false
  Arbitrary = false
  ArbitraryTolerances = false
  EqualTolerance = true
  ExtensionAngle = 0
  FormatSpec = %.2w
  FormatSpecOverTolerance = %+.2w
  FormatSpecUnderTolerance = %+.2w
  Inverted = false
  LineAngle = 0
  LockPosition = false
  MeasureType = 1
  OverTolerance = 0
  References2D = -> [ProjItem003]
  Rotation = 0
  ScaleType = 0
  TheoreticalExact = false
  Type = 0
  UnderTolerance = 0
  X = -89.4309
  Y = -64.7156
FEATURE [TechDraw::DrawViewBalloon] Balloon001
  BubbleShape = 3
  EndType = 0
  EndTypeScale = 1
  KinkLength = 5
  LockPosition = false
  OriginX = -335.414
  OriginY = -258.29
  Rotation = 0
  ScaleType = 0
  ShapeScale = 1
  SourceView = -> ProjItem003
  Text = Stretcher position
  TextWrapLen = -1
  X = -225.559
  Y = -158.972
FEATURE [TechDraw::DrawViewDimension] Dimension036
  AngleOverride = false
  Arbitrary = false
  ArbitraryTolerances = false
  EqualTolerance = true
  ExtensionAngle = 0
  FormatSpec = %.2w
  FormatSpecOverTolerance = %+.2w
  FormatSpecUnderTolerance = %+.2w
  Inverted = false
  LineAngle = 0
  LockPosition = false
  MeasureType = 1
  OverTolerance = 0
  References2D = -> [ProjItem003]
  Rotation = 0
  ScaleType = 0
  TheoreticalExact = false
  Type = 0
  UnderTolerance = 0
  X = -69.6577
  Y = -65.0956
FEATURE [TechDraw::DrawViewDimension] Dimension037
  AngleOverride = false
  Arbitrary = false
  ArbitraryTolerances = false
  EqualTolerance = true
  ExtensionAngle = 0
  FormatSpec = %.0w
  FormatSpecOverTolerance = %+.2w
  FormatSpecUnderTolerance = %+.2w
  Inverted = false
  LineAngle = 0
  LockPosition = false
  MeasureType = 1
  OverTolerance = 0
  References2D = -> [ProjItem003]
  Rotation = 0
  ScaleType = 0
  TheoreticalExact = false
  Type = 0
  UnderTolerance = 0
  X = -102.646
  Y = -74.6329
FEATURE [TechDraw::DrawViewDimension] Dimension038
  AngleOverride = false
  Arbitrary = false
  ArbitraryTolerances = false
  EqualTolerance = true
  ExtensionAngle = 0
  FormatSpec = %.2w
  FormatSpecOverTolerance = %+.2w
  FormatSpecUnderTolerance = %+.2w
  Inverted = false
  LineAngle = 0
  LockPosition = false
  MeasureType = 1
  OverTolerance = 0
  References2D = -> [View002]
  Rotation = 0
  ScaleType = 0
  TheoreticalExact = false
  Type = 0
  UnderTolerance = 0
  X = -54.9068
  Y = 183.126
FEATURE [TechDraw::DrawPage] Page  label="SideDrillTemplate"
  KeepUpdated = true
  NextBalloonIndex = 1
  ProjectionType = 0
  Template = -> Template
  Views = -> [View002,Dimension,Dimension038]
FEATURE [App::Part] Part  label="TheChair"
  Origin = -> Origin003
FEATURE [PartDesign::Boolean] Boolean
  Group = -> [Body,Clone,Body002,PathArray,PathArray001]
  Type = 0
FEATURE [PartDesign::Body] Body003  label="FusedChair"
  Group = -> [Boolean]
  Origin = -> Origin004
  Tip = -> Boolean
FEATURE [TechDraw::DrawViewDimension] Dimension039
  AngleOverride = false
  Arbitrary = false
  ArbitraryTolerances = false
  EqualTolerance = true
  ExtensionAngle = 0
  FormatSpec = %.0w
  FormatSpecOverTolerance = %+.2w
  FormatSpecUnderTolerance = %+.2w
  Inverted = false
  LineAngle = 0
  LockPosition = false
  MeasureType = 1
  OverTolerance = 0
  References2D = -> [ProjItem003]
  Rotation = 0
  ScaleType = 0
  TheoreticalExact = false
  Type = 0
  UnderTolerance = 0
  X = 49.2696
  Y = -37.4246
FEATURE [TechDraw::DrawPage] Page002  label="Cuts"
  KeepUpdated = true
  NextBalloonIndex = 4
  ProjectionType = 0
  Template = -> Template002
  Views = -> [ProjGroup001,Dimension009,Dimension010,Dimension011,Dimension012,Dimension013,Dimension014,Dimension015,Dimension016,Dimension017,Dimension018,Dimension019,Dimension020,Dimension021,Dimension022,Dimension023,Dimension024,Dimension025,Dimension026,Dimension027,Dimension033,Balloon,Dimension034,Dimension035,Balloon001,Dimension036,Dimension037,Dimension039]
note: 3 file-system paths scrubbed to <path> (originals preserved in the JSON sidecar)
